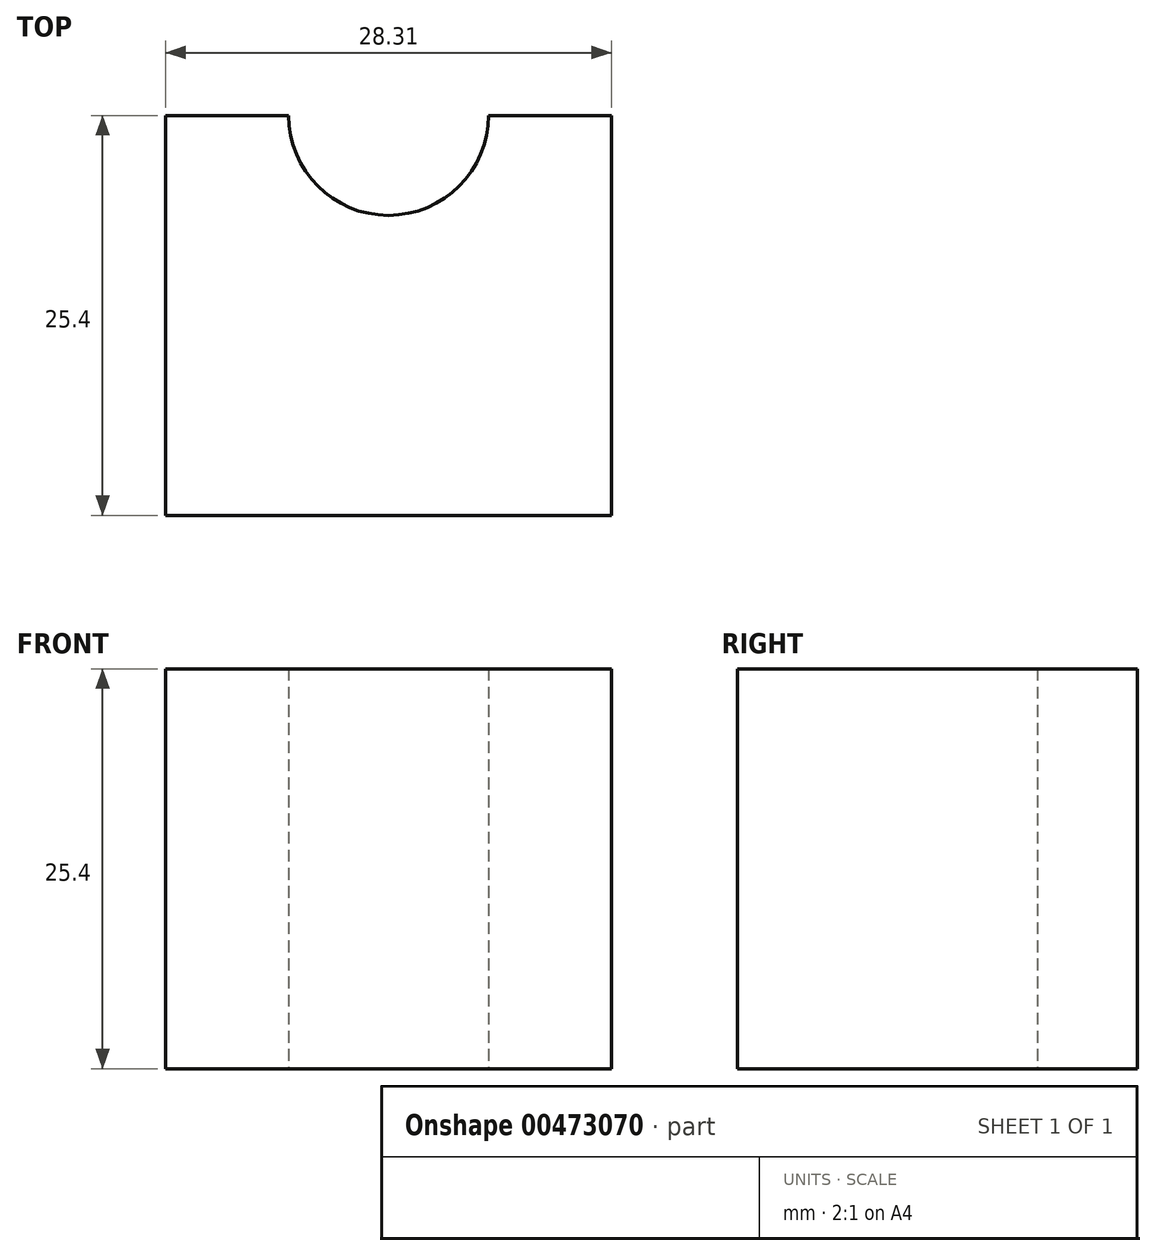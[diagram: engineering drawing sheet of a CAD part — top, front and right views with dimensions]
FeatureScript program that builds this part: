
annotation { "Feature Type Name" : "Feature", "Feature Type Description" : "" }
export const myFeature = defineFeature(function(context is Context, id is Id, definition is map)
    precondition{}
    {
        {
            var Q0;
            Q0=qCreatedBy(makeId("Top.planeOp"),FACE);
            var sketch = newSketch(context, id + "F0", { "sketchPlane" : qUnion([Q0])});
            skLineSegment(sketch, "E0.bottom", {"start": v(0, 0) * mm, "end": v(28.3, 0) * mm});
            skLineSegment(sketch, "E0.top", {"start": v(0, 25.4) * mm, "end": v(28.3, 25.4) * mm});
            skLineSegment(sketch, "E0.left", {"start": v(0, 0) * mm, "end": v(0, 25.4) * mm});
            skLineSegment(sketch, "E0.right", {"start": v(28.3, 0) * mm, "end": v(28.3, 25.4) * mm});
            skArc(sketch, "E1", {"start": v(0, 25.4) * mm, "mid": v(14.15, 39.55) * mm, "end": v(28.3, 25.4) * mm});
            skCircle(sketch, "E2", {"center": v(14.15, 25.4) * mm, "radius": 6.35 * mm});
            skSolve(sketch);
        }
        {
            var Q0;
            Q0=makeQuery(id+"F0.imprint","IMPRINT",FACE,{"disambiguationData":[TD([[makeQuery(id+"F0.imprint","IMPRINT",EDGE,{"derivedFrom":sQuery(id+"F0.wireOp",EDGE,"E0.bottom")}),1.0]])]});
            var Q1;
            {var subQ0=sQuery(id+"F0.wireOp",EDGE,"E1");Q1=makeQuery(id+"F0.imprint","IMPRINT",FACE,{"disambiguationData":[TD([[makeQuery(id+"F0.imprint","IMPRINT",EDGE,{"derivedFrom":subQ0}),-1.0]])]});}
            extrude(context, id + "F1", {"entities" : qUnion([Q0, Q1]), "depth" : 25.4 * mm});
        }
    });
